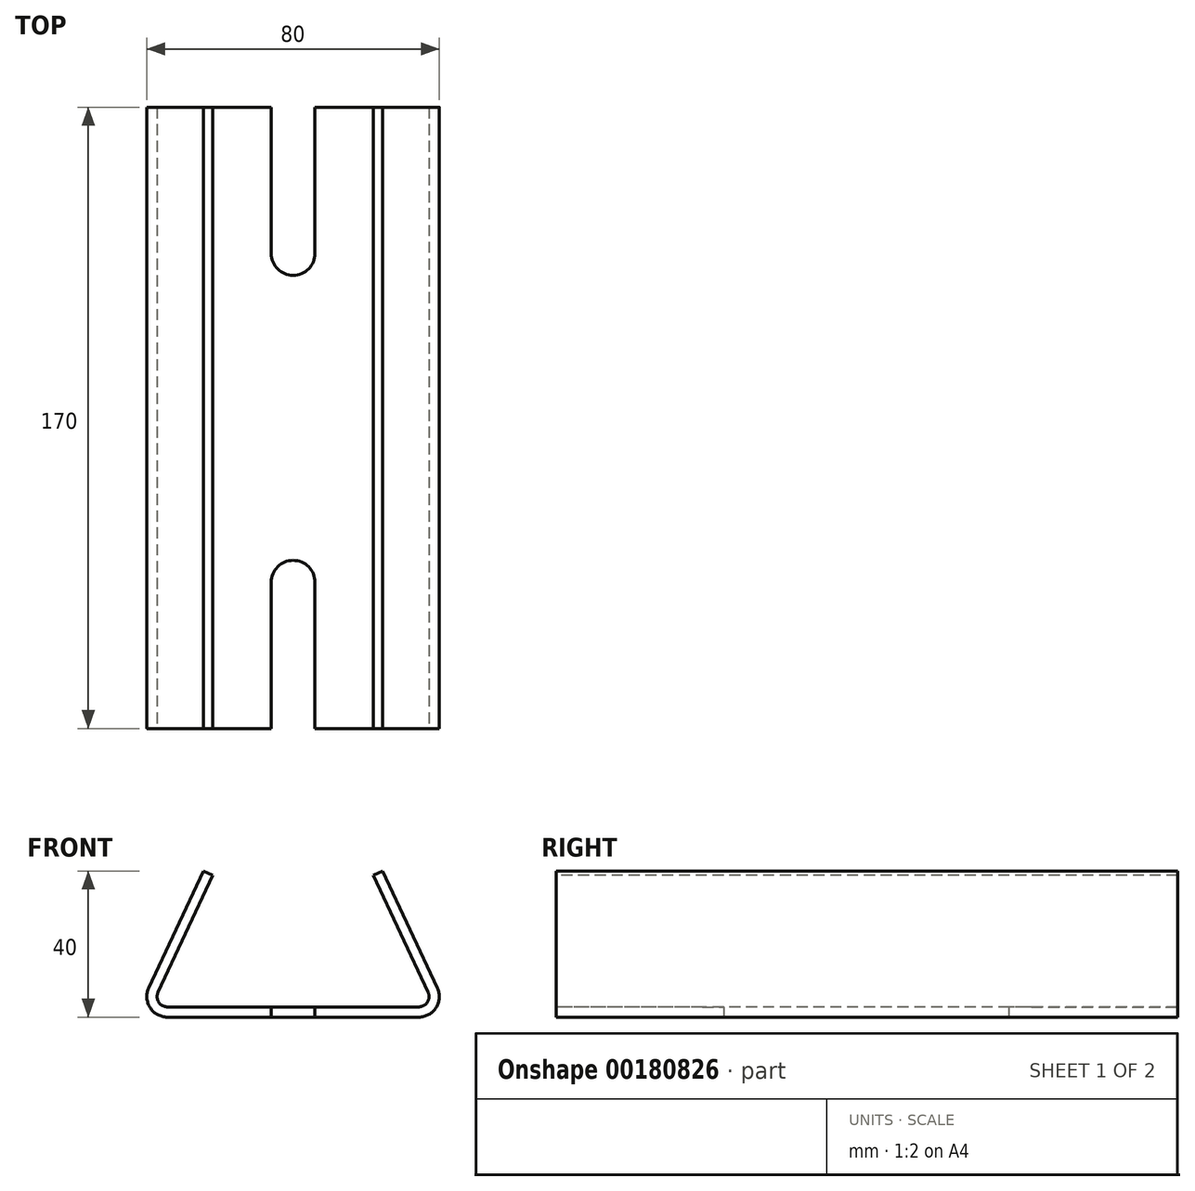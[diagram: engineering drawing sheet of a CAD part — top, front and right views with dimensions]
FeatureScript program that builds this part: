
annotation { "Feature Type Name" : "Feature", "Feature Type Description" : "" }
export const myFeature = defineFeature(function(context is Context, id is Id, definition is map)
    precondition{}
    {
        {
            var Q0;
            Q0=qCreatedBy(makeId("Front.planeOp"),FACE);
            var sketch = newSketch(context, id + "F0", { "sketchPlane" : qUnion([Q0])});
            skLineSegment(sketch, "E0", {"start": v(3.71, 7.97) * mm, "end": v(18.65, 40) * mm});
            skPoint(sketch, "E1.visualSharp", {"position": v(0, 0) * mm});
            skArc(sketch, "E1.filletArc", {"start": v(3.71, 7.97) * mm, "mid": v(4.07, 2.6) * mm, "end": v(8.8, 0) * mm});
            skLineSegment(sketch, "E2.MirrorCS", {"start": v(82.66, 7.97) * mm, "end": v(67.73, 40) * mm});
            skArc(sketch, "E3.MirrorCS", {"start": v(82.66, 7.97) * mm, "mid": v(82.31, 2.6) * mm, "end": v(77.6, 0) * mm});
            skLineSegment(sketch, "E4", {"start": v(8.8, 0) * mm, "end": v(77.6, 0) * mm});
            skLineSegment(sketch, "E5.0", {"start": v(6.25, 6.78) * mm, "end": v(21.19, 38.82) * mm});
            skArc(sketch, "E6.filletArc", {"start": v(6.25, 6.78) * mm, "mid": v(6.43, 4.1) * mm, "end": v(8.8, 2.8) * mm});
            skLineSegment(sketch, "E7.MirrorCS", {"start": v(80.13, 6.78) * mm, "end": v(65.19, 38.82) * mm});
            skArc(sketch, "E8.MirrorCS", {"start": v(80.13, 6.78) * mm, "mid": v(79.95, 4.1) * mm, "end": v(77.6, 2.8) * mm});
            skLineSegment(sketch, "E9", {"start": v(8.8, 2.8) * mm, "end": v(77.6, 2.8) * mm});
            skLineSegment(sketch, "E10", {"start": v(21.19, 38.82) * mm, "end": v(18.65, 40) * mm});
            skLineSegment(sketch, "E11.MirrorCS", {"start": v(65.19, 38.82) * mm, "end": v(67.73, 40) * mm});
            skSolve(sketch);
        }
        {
            var Q0;
            Q0 = qSketchRegion(id + "F0", true);
            extrude(context, id + "F1", {"entities" : qUnion([Q0]), "endBound" : BoundingType.SYMMETRIC, "oppositeDirection" : true, "depth" : 170 * mm});
        }
        {
            var Q0;
            Q0=makeQuery(id+"F1.opExtrude","SWEPT_FACE",FACE,{"disambiguationData":[OSD([sQuery(id+"F0.wireOp",EDGE,"E9")])]});
            var sketch = newSketch(context, id + "F2", { "sketchPlane" : qUnion([Q0])});
            skLineSegment(sketch, "E12", {"start": v(49.2, -45) * mm, "end": v(49.2, -85) * mm});
            skLineSegment(sketch, "E13.MirrorCS", {"start": v(37.2, -45) * mm, "end": v(37.2, -85) * mm});
            skArc(sketch, "E14", {"start": v(49.2, -45) * mm, "mid": v(43.2, -39) * mm, "end": v(37.2, -45) * mm});
            skPoint(sketch, "E15.start.orphan", {"position": v(43.2, -85) * mm});
            skLineSegment(sketch, "E16", {"start": v(37.2, -85) * mm, "end": v(49.2, -85) * mm});
            skLineSegment(sketch, "E17.MirrorCS", {"start": v(49.2, 45) * mm, "end": v(49.2, 85) * mm});
            skArc(sketch, "E18.MirrorCS", {"start": v(49.2, 45) * mm, "mid": v(43.2, 39) * mm, "end": v(37.2, 45) * mm});
            skLineSegment(sketch, "E19.MirrorCS", {"start": v(37.2, 45) * mm, "end": v(37.2, 85) * mm});
            skLineSegment(sketch, "E20.MirrorCS", {"start": v(37.2, 85) * mm, "end": v(49.2, 85) * mm});
            skSolve(sketch);
        }
        {
            var Q0;
            Q0=makeQuery(id+"F2.imprint","IMPRINT",FACE,{"disambiguationData":[TD([[makeQuery(id+"F2.imprint","IMPRINT",EDGE,{"derivedFrom":sQuery(id+"F2.wireOp",EDGE,"E12")}),-1.0]])]});
            var Q1;
            Q1=makeQuery(id+"F2.imprint","IMPRINT",FACE,{"disambiguationData":[TD([[makeQuery(id+"F2.imprint","IMPRINT",EDGE,{"derivedFrom":sQuery(id+"F2.wireOp",EDGE,"E17.MirrorCS")}),1.0]])]});
            extrude(context, id + "F3", {"entities" : qUnion([Q0, Q1]), "operationType" : NewBodyOperationType.REMOVE, "endBound" : BoundingType.THROUGH_ALL, "oppositeDirection" : true, "depth" : 25 * mm});
        }
    });
